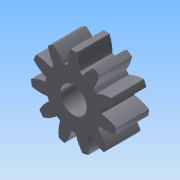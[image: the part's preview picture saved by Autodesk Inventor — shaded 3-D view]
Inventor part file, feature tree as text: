
AUTODESK INVENTOR PART (.ipt)
format: ipt  version: 2015 SP1 (Build 190203100, 203)  size: 177,664 bytes
history: native  units: mm (DEFAULTED — no unit token found)
features: plane x3, other x3, sketch x2, extrude x1, hole x1
ambient origin geometry x8: Origin, YZ Plane, XZ Plane, XY Plane, X Axis, Y Axis, Z Axis, Center Point
bodies: Solid1 (feature_tree)
feature tree (10):
  extrude  "Extrusion1"  Depth=6.35mm TaperAngle=0.0deg
  plane  "Work Plane1"
  plane  "Work Plane2"
  plane  "Work Plane3"
  other  "Spur Gear"
  hole  "Hole1"  [1 undecoded]
  sketch  "Sketch1"  dims[d0=16.51mm d1=6.35mm d2=0.0mm]
  sketch  "Sketch2"  dims[d3=13.97mm d4=76.2mm d5=0.0mm d6=0.0mm d7=2.855993mm d9=0.0mm d14=0.0mm d15=41.91mm d16=0.0mm d17=0.0mm d18=0.0mm d19=41.91mm d20=25.4mm d21=25.4mm d22=5.0546mm d23=19.05mm d24=9.525mm d25=6.35mm d26=14.3117mm d27=25.4mm d28=20.594885mm]
  other  "Srf1"
  other  "Pitch Diameter"
note: 1 required parameter value undecoded (feature->parameter linkage not recoverable at this tier; creation-order binding heuristic only, values carry confidence <= 0.55)
